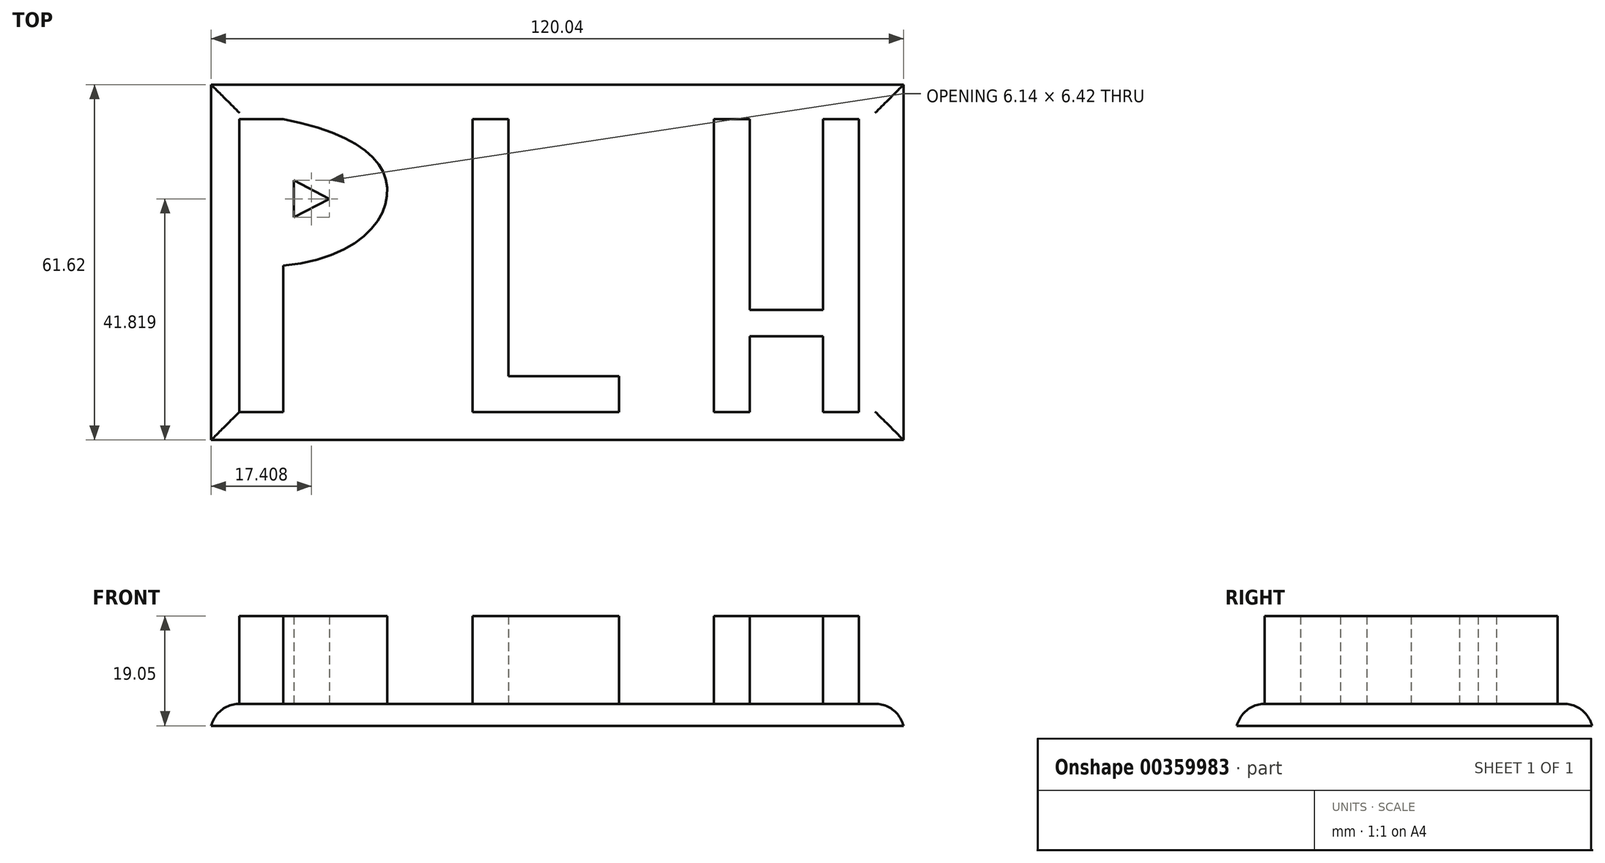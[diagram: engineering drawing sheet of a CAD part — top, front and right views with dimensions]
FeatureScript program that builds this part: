
annotation { "Feature Type Name" : "Feature", "Feature Type Description" : "" }
export const myFeature = defineFeature(function(context is Context, id is Id, definition is map)
    precondition{}
    {
        {
            var Q0;
            Q0=qCreatedBy(makeId("Top.planeOp"),FACE);
            var sketch = newSketch(context, id + "F0", { "sketchPlane" : qUnion([Q0])});
            skFitSpline(sketch, "E0", {"points": [v(-58.25, 33.08) * mm, v(-40.2, 20.52) * mm, v(-58.25, 7.68) * mm], "startDerivative": vector(76.53, -14.35) * mm, "endDerivative": vector(-74.07, -7.05) * mm});
            skLineSegment(sketch, "E1", {"start": v(-58.25, -17.72) * mm, "end": v(-65.87, -17.72) * mm});
            skLineSegment(sketch, "E2", {"start": v(-65.87, -17.72) * mm, "end": v(-65.87, 33.08) * mm});
            skLineSegment(sketch, "E3", {"start": v(-65.87, 33.08) * mm, "end": v(-58.25, 33.08) * mm});
            skLineSegment(sketch, "E4", {"start": v(-58.25, 7.68) * mm, "end": v(-58.25, -17.72) * mm});
            skLineSegment(sketch, "E5", {"start": v(-56.38, 22.47) * mm, "end": v(-56.38, 16.05) * mm});
            skLineSegment(sketch, "E6", {"start": v(-56.38, 16.05) * mm, "end": v(-50.24, 19.26) * mm});
            skPoint(sketch, "E6.endSnap0", {"position": v(-56.38, 19.26) * mm});
            skLineSegment(sketch, "E7", {"start": v(-50.24, 19.26) * mm, "end": v(-56.38, 22.47) * mm});
            skLineSegment(sketch, "E8.bottom", {"start": v(-25.4, 33.08) * mm, "end": v(-19.18, 33.08) * mm});
            skLineSegment(sketch, "E8.top", {"start": v(-25.4, -17.72) * mm, "end": v(-19.18, -17.72) * mm});
            skLineSegment(sketch, "E8.left", {"start": v(-25.4, 33.08) * mm, "end": v(-25.4, -17.72) * mm});
            skLineSegment(sketch, "E8.right", {"start": v(-19.18, 33.08) * mm, "end": v(-19.18, -17.72) * mm});
            skLineSegment(sketch, "E9.bottom", {"start": v(-25.4, -11.5) * mm, "end": v(0, -11.5) * mm});
            skLineSegment(sketch, "E9.top", {"start": v(-25.4, -17.72) * mm, "end": v(0, -17.72) * mm});
            skLineSegment(sketch, "E9.left", {"start": v(-25.4, -11.5) * mm, "end": v(-25.4, -17.72) * mm});
            skLineSegment(sketch, "E9.right", {"start": v(0, -11.5) * mm, "end": v(0, -17.72) * mm});
            skPoint(sketch, "E10", {"position": v(-19.18, -11.5) * mm});
            skPoint(sketch, "E11", {"position": v(-28.75, 26.38) * mm});
            skLineSegment(sketch, "E12", {"start": v(16.47, 33.08) * mm, "end": v(16.47, -17.72) * mm});
            skLineSegment(sketch, "E13", {"start": v(16.47, 33.08) * mm, "end": v(22.7, 33.08) * mm});
            skLineSegment(sketch, "E14", {"start": v(22.7, -17.72) * mm, "end": v(16.47, -17.72) * mm});
            skLineSegment(sketch, "E15", {"start": v(22.7, 0) * mm, "end": v(35.4, 0) * mm});
            skLineSegment(sketch, "E16", {"start": v(35.4, 0) * mm, "end": v(35.4, 33.08) * mm});
            skLineSegment(sketch, "E17", {"start": v(35.4, 33.08) * mm, "end": v(41.61, 33.08) * mm});
            skLineSegment(sketch, "E18", {"start": v(41.61, 33.08) * mm, "end": v(41.61, -17.72) * mm});
            skLineSegment(sketch, "E19", {"start": v(41.61, -17.72) * mm, "end": v(35.4, -17.72) * mm});
            skLineSegment(sketch, "E20", {"start": v(35.4, -17.72) * mm, "end": v(35.4, -4.57) * mm});
            skLineSegment(sketch, "E21", {"start": v(35.4, -4.57) * mm, "end": v(22.7, -4.57) * mm});
            skLineSegment(sketch, "E22", {"start": v(22.7, -4.57) * mm, "end": v(22.7, -17.72) * mm});
            skLineSegment(sketch, "E23", {"start": v(22.7, 33.08) * mm, "end": v(22.7, 0) * mm});
            skSolve(sketch);
        }
        {
            var Q0;
            Q0=makeQuery(id+"F0.imprint","IMPRINT",FACE,{"disambiguationData":[TD([[makeQuery(id+"F0.imprint","IMPRINT",EDGE,{"derivedFrom":sQuery(id+"F0.wireOp",EDGE,"E0")}),-1.0]])]});
            extrude(context, id + "F1", {"entities" : qUnion([Q0]), "depth" : 15.24 * mm});
        }
        {
            var Q0;
            Q0 = qSketchRegion(id + "F0", true);
            extrude(context, id + "F2", {"entities" : qUnion([Q0]), "operationType" : NewBodyOperationType.ADD, "depth" : 15.24 * mm});
        }
        {
            var Q0;
            Q0=qCreatedBy(makeId("Top.planeOp"),FACE);
            var sketch = newSketch(context, id + "F3", { "sketchPlane" : qUnion([Q0])});
            skLineSegment(sketch, "E24", {"start": v(49.32, 32.31) * mm, "end": v(49.32, -17.52) * mm});
            skLineSegment(sketch, "E25.bottom", {"start": v(-70.72, 39.06) * mm, "end": v(49.32, 39.06) * mm});
            skLineSegment(sketch, "E25.top", {"start": v(-70.72, -22.56) * mm, "end": v(49.32, -22.56) * mm});
            skLineSegment(sketch, "E25.left", {"start": v(-70.72, 39.06) * mm, "end": v(-70.72, -22.56) * mm});
            skLineSegment(sketch, "E25.right", {"start": v(49.32, 39.06) * mm, "end": v(49.32, -22.56) * mm});
            skSolve(sketch);
        }
        {
            var Q0;
            Q0 = qSketchRegion(id + "F3", true);
            extrude(context, id + "F4", {"entities" : qUnion([Q0]), "oppositeDirection" : true, "depth" : 3.8 * mm});
        }
        {
            var Q0;
            Q0=makeQuery(id+"F4.opExtrude","CAP_EDGE",EDGE,{"disambiguationData":[OSD([sQuery(id+"F3.wireOp",EDGE,"E25.top")])],"isStart":true});
            var Q1;
            Q1=makeQuery(id+"F4.opExtrude","CAP_EDGE",EDGE,{"disambiguationData":[OSD([sQuery(id+"F3.wireOp",EDGE,"E25.left")])],"isStart":true});
            var Q2;
            Q2=makeQuery(id+"F4.opExtrude","CAP_EDGE",EDGE,{"disambiguationData":[OSD([sQuery(id+"F3.wireOp",EDGE,"E25.right")])],"isStart":true});
            var Q3;
            Q3=makeQuery(id+"F4.opExtrude","CAP_EDGE",EDGE,{"disambiguationData":[OSD([sQuery(id+"F3.wireOp",EDGE,"E25.bottom")])],"isStart":true});
            fillet(context, id + "F5", {"entities" : qUnion([Q0, Q1, Q2, Q3]), "radius" : 5.08 * mm, "tangentPropagation" : true, "allowEdgeOverflow" : false});
        }
    });
